# Revit family: Hager-Orion_Inox-IP66-D210-Cl.I-Inox_encl-630A-600mm-CH-it
name_source: partatom
category: Equipement électrique
units: mm (PartAtom-declared; Revit-internal decimal feet)

## family parameters
Configuration du panneau = Deux colonnes, circuits au sein
Cote de connecteur circulaire = Utiliser le diamètre
Couper avec des vides une fois chargée = Non
Hôte = Face
Partagée = Non
Point de calcul de pièce = Non
Type d'élément = Tableau de raccordement

## types (12) — shared parameters
Commentaires du type = Orion Inox
EF000003 - Tipo di montaggio = EV000384 - A parete
EF000007 - colore = EV000154 - altri
EF000040 - Altezza = 600 mm
EF000049 - profondità = 210 mm  [stored 0.688976 ft]
EF000118 - con piastra di montaggio = Non
EF000339 - tipo di copertura = EV004216 - porta
EF001088 - possibilità di applicazione = Oui
EF001131 - profondità interna = 176 mm
EF001596 - Attacco Lampada = EV000166 - acciaio inossidabile
EF003532 - adatto per uso esterno = Oui
EF004464 - tipo di porta = EV002646 - singolo
EF005474 - grado di protezione (IP) = EV006422 - IP66
EF007800 - adatto per parafulmine = Non
EF008873 - corrente nominale (In) = 630 A
EF009170 - spessore materiale scatola = 2 mm  [stored 0.00656168 ft]
EF009171 - spessore materiale porta/coperchio = 2 mm  [stored 0.00656168 ft]
EF015940 - Coprire con rilascio di sovrapressione = Non
Fabricant = Hager
HG000002 - Con porta = Oui
HG000003 - Gamma = Orion Inox
HG000006 - Ad incasso = Non
HG000009 - Porta doppia a battente = Non
HG000010 - Porte asimmetriche = Non
HG000023 - Custodia a doppia sezione = Non
HG000024 - Altezza della sezione inferiore = 800 mm  [stored 2.62467 ft]
HG000026 - A pavimento = Non
zero-valued in all types: EF000218 - profondità di incasso, EF000266 - numero di file, EF000437 - numero di ingressi per conduttori, EF002950 - Numero moduli DIN, EF004427 - numero di moduli, EF009554 - numero delle aperture per la piastra della flangia, Elévation par défaut, HG000027 - Altezza dello zoccolo

## per-type parameters (varying)
| type | EF000008 - Larghezza | EF001613 - Integrità del circuito | EF004293 - resistenza agli urti | EF006244 - coperchio/porta trasparente | EF006306 - con serratura | EF009212 - esecuzione coperchio | HG000004 - Codice produttore |
| A parete IP66 L400 A600 P210  - FL025BWL | 400 mm  [stored 1.31234 ft] |  | EV008784 - IK10 | Non | Non | EV009916 - con taglio | FL025BWL |
| A parete IP66 L400 A600 P210  - FL025TW | 400 mm  [stored 1.31234 ft] | EV000494 - senza | EV006814 - IK08 | Oui | Oui | EV000116 - chiuso | FL025TW |
| A parete IP66 L400 A600 P210  - FL025TWL | 400 mm  [stored 1.31234 ft] | EV000494 - senza | EV006814 - IK08 | Oui | Oui | EV000116 - chiuso | FL025TWL |
| A parete IP66 L500 A600 P210  - FL027BW | 500 mm  [stored 1.64042 ft] | EV000494 - senza | EV008784 - IK10 | Non | Oui | EV000116 - chiuso | FL027BW |
| A parete IP66 L500 A600 P210  - FL027BWL | 500 mm  [stored 1.64042 ft] | EV000494 - senza | EV008784 - IK10 | Non | Oui | EV000116 - chiuso | FL027BWL |
| A parete IP66 L500 A600 P210  - FL027TW | 500 mm  [stored 1.64042 ft] | EV000494 - senza | EV006814 - IK08 | Oui | Oui | EV000116 - chiuso | FL027TW |
| A parete IP66 L500 A600 P210  - FL027TWL | 500 mm  [stored 1.64042 ft] | EV000494 - senza | EV006814 - IK08 | Oui | Oui | EV000116 - chiuso | FL027TWL |
| A parete IP66 L600 A600 P210  - FL025BW | 600 mm |  | EV008784 - IK10 | Non | Non | EV009916 - con taglio | FL025BW |
| A parete IP66 L600 A600 P210  - FL028BW | 600 mm | EV000494 - senza | EV008784 - IK10 | Non | Oui | EV000116 - chiuso | FL028BW |
| A parete IP66 L600 A600 P210  - FL028BWL | 600 mm | EV000494 - senza | EV008784 - IK10 | Non | Oui | EV000116 - chiuso | FL028BWL |
| A parete IP66 L600 A600 P210  - FL028TW | 600 mm | EV000494 - senza | EV006814 - IK08 | Oui | Oui | EV000116 - chiuso | FL028TW |
| A parete IP66 L600 A600 P210  - FL028TWL | 600 mm | EV000494 - senza | EV006814 - IK08 | Oui | Oui | EV000116 - chiuso | FL028TWL |

note: [stored X ft] marks values corroborated as IEEE doubles in the binary element streams (Revit-internal decimal feet)

## geometry (parser evidence)
native form markers: Sweep x8
no freeform markers — native parametric forms only
